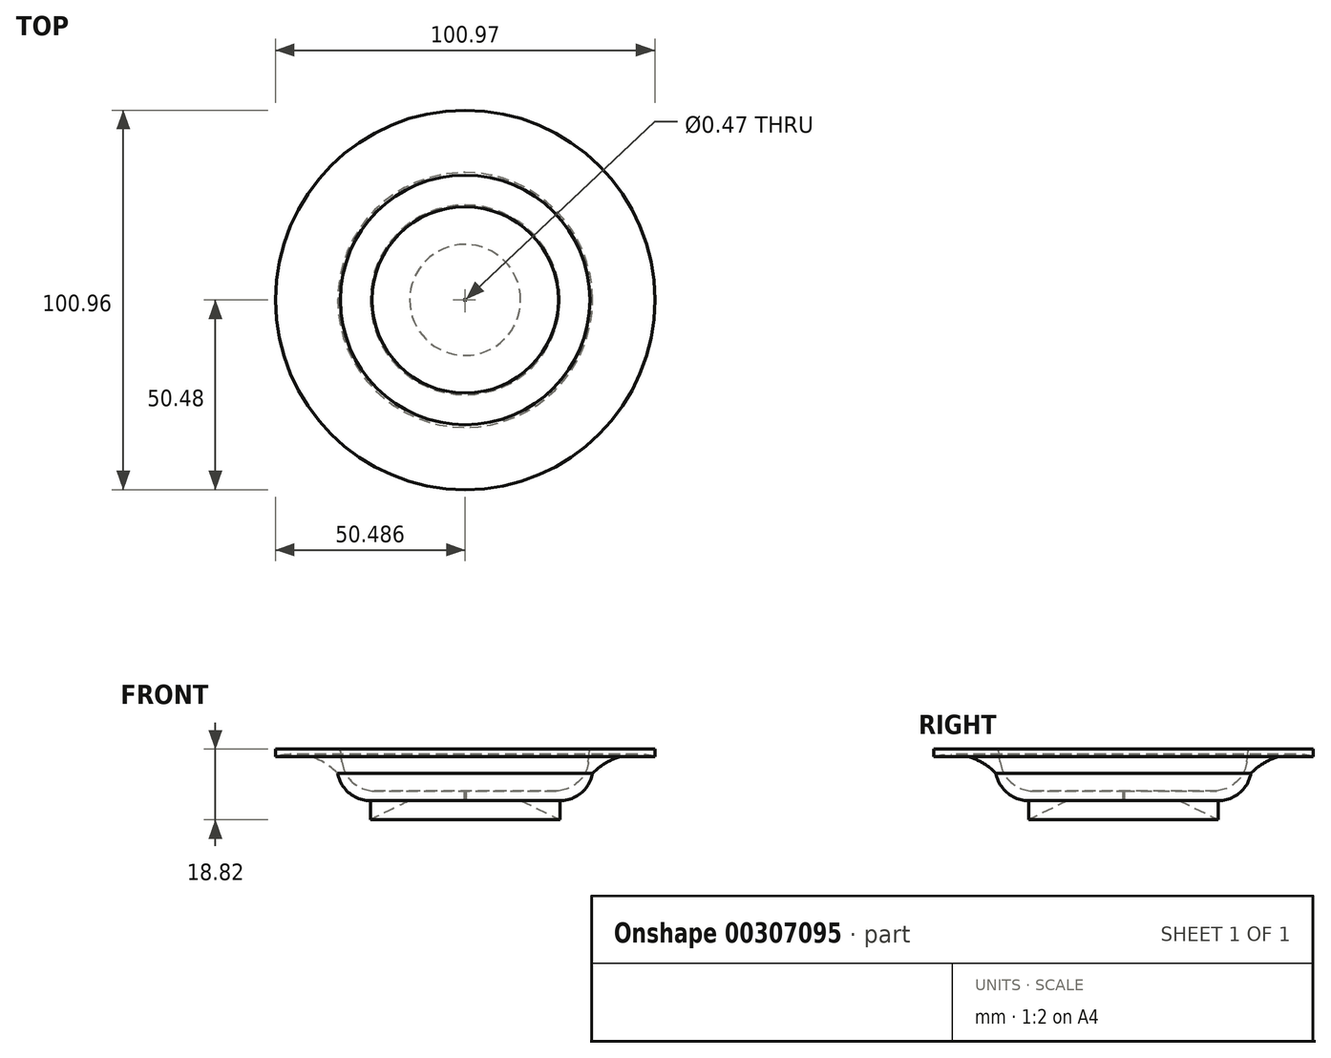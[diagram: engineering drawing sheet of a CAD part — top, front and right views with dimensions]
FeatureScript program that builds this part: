
annotation { "Feature Type Name" : "Feature", "Feature Type Description" : "" }
export const myFeature = defineFeature(function(context is Context, id is Id, definition is map)
    precondition{}
    {
        {
            var Q0;
            Q0=qCreatedBy(makeId("Front.planeOp"),FACE);
            var sketch = newSketch(context, id + "F0", { "sketchPlane" : qUnion([Q0])});
            skLineSegment(sketch, "E0", {"start": v(4.52, 10) * mm, "end": v(29.52, 10) * mm});
            skLineSegment(sketch, "E1", {"start": v(29.52, 10) * mm, "end": v(29.52, 4.92) * mm});
            skArc(sketch, "E2", {"start": v(29.52, 10) * mm, "mid": v(35.17, 12.05) * mm, "end": v(38.2, 17.25) * mm});
            skLineSegment(sketch, "E3", {"start": v(4.52, 12.62) * mm, "end": v(29.52, 12.62) * mm});
            skArc(sketch, "E4", {"start": v(27.86, 12.6) * mm, "mid": v(33.99, 14.64) * mm, "end": v(37.07, 20.32) * mm});
            skLineSegment(sketch, "E5", {"start": v(4.52, 10) * mm, "end": v(4.52, 12.62) * mm});
            skLineSegment(sketch, "E6", {"start": v(29.52, 4.92) * mm, "end": v(19.05, 10) * mm});
            skArc(sketch, "E7", {"start": v(54.77, 21.67) * mm, "mid": v(45.86, 21.78) * mm, "end": v(38.2, 17.25) * mm});
            skLineSegment(sketch, "E8", {"start": v(37.07, 20.32) * mm, "end": v(37.5, 23.74) * mm});
            skLineSegment(sketch, "E9", {"start": v(37.5, 23.74) * mm, "end": v(54.77, 23.74) * mm});
            skLineSegment(sketch, "E10", {"start": v(54.77, 23.74) * mm, "end": v(54.77, 21.67) * mm});
            skSolve(sketch);
        }
        {
            var Q0;
            Q0=qCreatedBy(makeId("Front.planeOp"),FACE);
            var sketch = newSketch(context, id + "F1", { "sketchPlane" : qUnion([Q0])});
            skLineSegment(sketch, "E11", {"start": v(4.29, 10) * mm, "end": v(4.29, -25) * mm});
            skLineSegment(sketch, "E12", {"start": v(4.29, -25) * mm, "end": v(4.29, 55.48) * mm});
            skSolve(sketch);
        }
        {
            var Q0;
            Q0 = qSketchRegion(id + "F0", true);
            var Q1;
            Q1=sQuery(id+"F1.wireOp",EDGE,"E12");
            revolve(context, id + "F2", {"entities" : qUnion([Q0]), "axis" : qUnion([Q1]), "revolveType" : RevolveType.FULL});
        }
    });
